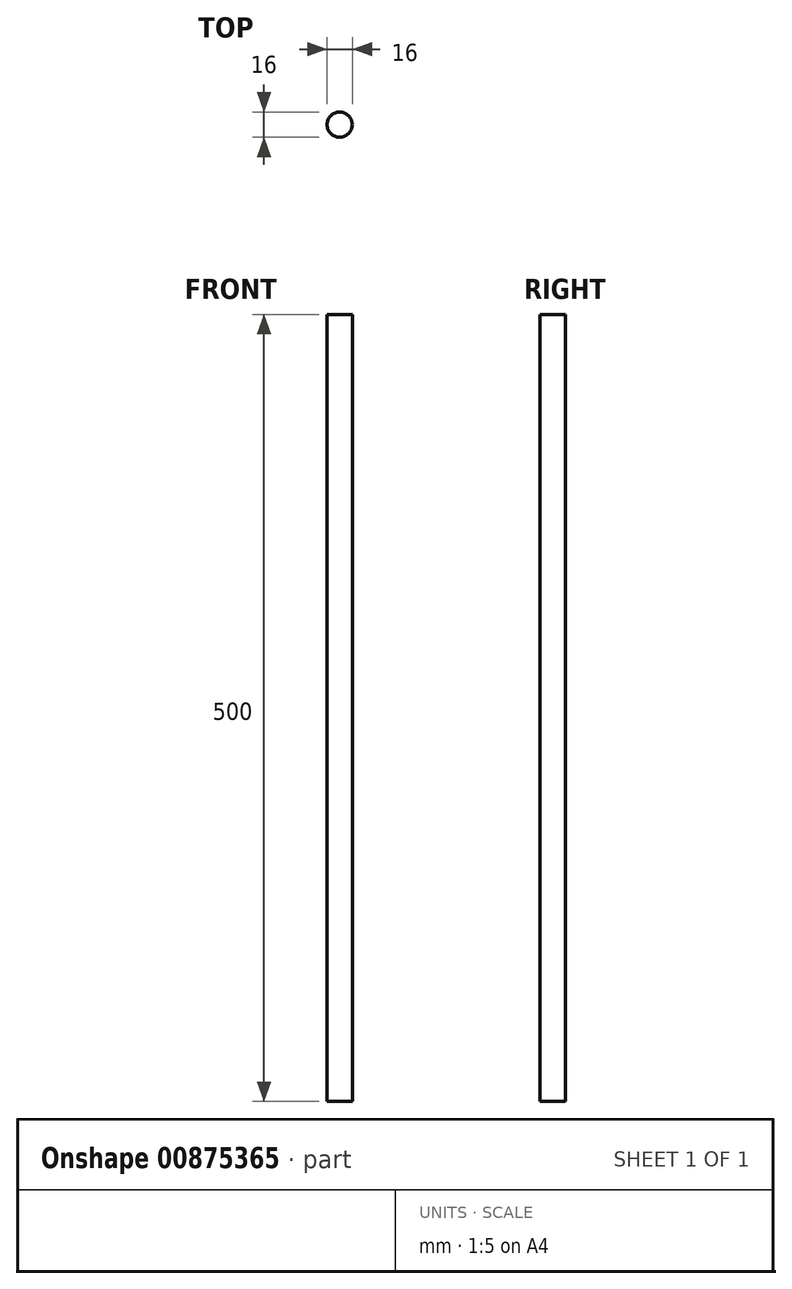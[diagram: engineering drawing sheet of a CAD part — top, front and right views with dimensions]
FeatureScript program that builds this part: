
annotation { "Feature Type Name" : "Feature", "Feature Type Description" : "" }
export const myFeature = defineFeature(function(context is Context, id is Id, definition is map)
    precondition{}
    {
        {
            var Q0;
            Q0=qCreatedBy(makeId("Top.planeOp"),FACE);
            var sketch = newSketch(context, id + "F0", { "sketchPlane" : qUnion([Q0])});
            skCircle(sketch, "E0", {"center": v(0, 0) * mm, "radius": 8 * mm});
            skSolve(sketch);
        }
        {
            var Q0;
            Q0=makeQuery(id+"F0.imprint","IMPRINT",FACE,{"disambiguationData":[TD([[makeQuery(id+"F0.imprint","IMPRINT",EDGE,{"derivedFrom":sQuery(id+"F0.wireOp",EDGE,"E0")}),1.0]])]});
            extrude(context, id + "F1", {"entities" : qUnion([Q0]), "depth" : 500 * mm, "offsetDistance" : 25 * mm});
        }
    });
